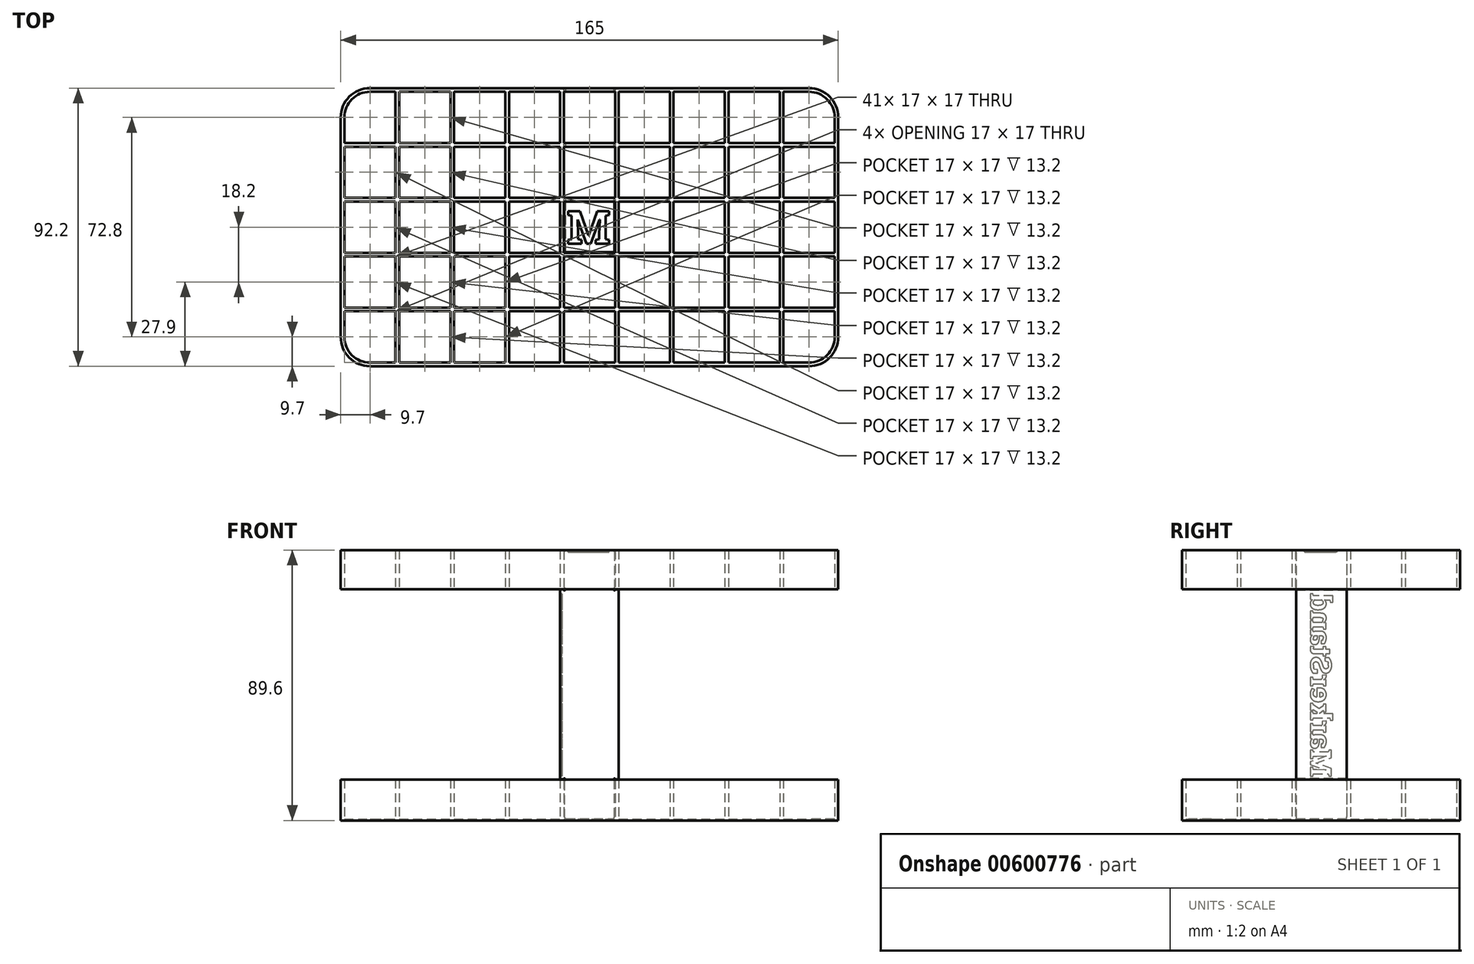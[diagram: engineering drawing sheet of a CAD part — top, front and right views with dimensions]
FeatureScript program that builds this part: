
annotation { "Feature Type Name" : "Feature", "Feature Type Description" : "" }
export const myFeature = defineFeature(function(context is Context, id is Id, definition is map)
    precondition{}
    {
        {
            var Q0;
            Q0=qCreatedBy(makeId("Top.planeOp"),FACE);
            var sketch = newSketch(context, id + "F0", { "sketchPlane" : qUnion([Q0])});
            skLineSegment(sketch, "E0.bottom", {"start": v(-82.5, 46.1) * mm, "end": v(82.5, 46.1) * mm});
            skLineSegment(sketch, "E0.top", {"start": v(-82.5, -46.1) * mm, "end": v(82.5, -46.1) * mm});
            skLineSegment(sketch, "E0.left", {"start": v(-82.5, 46.1) * mm, "end": v(-82.5, -46.1) * mm});
            skLineSegment(sketch, "E0.right", {"start": v(82.5, 46.1) * mm, "end": v(82.5, -46.1) * mm});
            skPoint(sketch, "E0.middle", {"position": v(0, 0) * mm});
            skLineSegment(sketch, "E1.bottom", {"start": v(-81.3, -44.9) * mm, "end": v(-64.3, -44.9) * mm});
            skLineSegment(sketch, "E1.top", {"start": v(-81.3, -27.9) * mm, "end": v(-64.3, -27.9) * mm});
            skLineSegment(sketch, "E1.left", {"start": v(-81.3, -44.9) * mm, "end": v(-81.3, -27.9) * mm});
            skLineSegment(sketch, "E1.right", {"start": v(-64.3, -44.9) * mm, "end": v(-64.3, -27.9) * mm});
            skLineSegment(sketch, "E2.0.1.0", {"start": v(-64.3, -26.7) * mm, "end": v(-64.3, -9.7) * mm});
            skLineSegment(sketch, "E2.0.1.1", {"start": v(-81.3, -26.7) * mm, "end": v(-64.3, -26.7) * mm});
            skLineSegment(sketch, "E2.0.1.2", {"start": v(-81.3, -26.7) * mm, "end": v(-81.3, -9.7) * mm});
            skLineSegment(sketch, "E2.0.1.3", {"start": v(-81.3, -9.7) * mm, "end": v(-64.3, -9.7) * mm});
            skLineSegment(sketch, "E2.0.2.0", {"start": v(-64.3, -8.5) * mm, "end": v(-64.3, 8.5) * mm});
            skLineSegment(sketch, "E2.0.2.1", {"start": v(-81.3, -8.5) * mm, "end": v(-64.3, -8.5) * mm});
            skLineSegment(sketch, "E2.0.2.2", {"start": v(-81.3, -8.5) * mm, "end": v(-81.3, 8.5) * mm});
            skLineSegment(sketch, "E2.0.2.3", {"start": v(-81.3, 8.5) * mm, "end": v(-64.3, 8.5) * mm});
            skLineSegment(sketch, "E2.0.3.0", {"start": v(-64.3, 9.7) * mm, "end": v(-64.3, 26.7) * mm});
            skLineSegment(sketch, "E2.0.3.1", {"start": v(-81.3, 9.7) * mm, "end": v(-64.3, 9.7) * mm});
            skLineSegment(sketch, "E2.0.3.2", {"start": v(-81.3, 9.7) * mm, "end": v(-81.3, 26.7) * mm});
            skLineSegment(sketch, "E2.0.3.3", {"start": v(-81.3, 26.7) * mm, "end": v(-64.3, 26.7) * mm});
            skLineSegment(sketch, "E2.0.4.0", {"start": v(-64.3, 27.9) * mm, "end": v(-64.3, 44.9) * mm});
            skLineSegment(sketch, "E2.0.4.1", {"start": v(-81.3, 27.9) * mm, "end": v(-64.3, 27.9) * mm});
            skLineSegment(sketch, "E2.0.4.2", {"start": v(-81.3, 27.9) * mm, "end": v(-81.3, 44.9) * mm});
            skLineSegment(sketch, "E2.0.4.3", {"start": v(-81.3, 44.9) * mm, "end": v(-64.3, 44.9) * mm});
            skLineSegment(sketch, "E2.1.0.0", {"start": v(-46.1, -44.9) * mm, "end": v(-46.1, -27.9) * mm});
            skLineSegment(sketch, "E2.1.0.1", {"start": v(-63.1, -44.9) * mm, "end": v(-46.1, -44.9) * mm});
            skLineSegment(sketch, "E2.1.0.2", {"start": v(-63.1, -44.9) * mm, "end": v(-63.1, -27.9) * mm});
            skLineSegment(sketch, "E2.1.0.3", {"start": v(-63.1, -27.9) * mm, "end": v(-46.1, -27.9) * mm});
            skLineSegment(sketch, "E2.1.1.0", {"start": v(-46.1, -26.7) * mm, "end": v(-46.1, -9.7) * mm});
            skLineSegment(sketch, "E2.1.1.1", {"start": v(-63.1, -26.7) * mm, "end": v(-46.1, -26.7) * mm});
            skLineSegment(sketch, "E2.1.1.2", {"start": v(-63.1, -26.7) * mm, "end": v(-63.1, -9.7) * mm});
            skLineSegment(sketch, "E2.1.1.3", {"start": v(-63.1, -9.7) * mm, "end": v(-46.1, -9.7) * mm});
            skLineSegment(sketch, "E2.1.2.0", {"start": v(-46.1, -8.5) * mm, "end": v(-46.1, 8.5) * mm});
            skLineSegment(sketch, "E2.1.2.1", {"start": v(-63.1, -8.5) * mm, "end": v(-46.1, -8.5) * mm});
            skLineSegment(sketch, "E2.1.2.2", {"start": v(-63.1, -8.5) * mm, "end": v(-63.1, 8.5) * mm});
            skLineSegment(sketch, "E2.1.2.3", {"start": v(-63.1, 8.5) * mm, "end": v(-46.1, 8.5) * mm});
            skLineSegment(sketch, "E2.1.3.0", {"start": v(-46.1, 9.7) * mm, "end": v(-46.1, 26.7) * mm});
            skLineSegment(sketch, "E2.1.3.1", {"start": v(-63.1, 9.7) * mm, "end": v(-46.1, 9.7) * mm});
            skLineSegment(sketch, "E2.1.3.2", {"start": v(-63.1, 9.7) * mm, "end": v(-63.1, 26.7) * mm});
            skLineSegment(sketch, "E2.1.3.3", {"start": v(-63.1, 26.7) * mm, "end": v(-46.1, 26.7) * mm});
            skLineSegment(sketch, "E2.1.4.0", {"start": v(-46.1, 27.9) * mm, "end": v(-46.1, 44.9) * mm});
            skLineSegment(sketch, "E2.1.4.1", {"start": v(-63.1, 27.9) * mm, "end": v(-46.1, 27.9) * mm});
            skLineSegment(sketch, "E2.1.4.2", {"start": v(-63.1, 27.9) * mm, "end": v(-63.1, 44.9) * mm});
            skLineSegment(sketch, "E2.1.4.3", {"start": v(-63.1, 44.9) * mm, "end": v(-46.1, 44.9) * mm});
            skLineSegment(sketch, "E2.2.0.0", {"start": v(-27.9, -44.9) * mm, "end": v(-27.9, -27.9) * mm});
            skLineSegment(sketch, "E2.2.0.1", {"start": v(-44.9, -44.9) * mm, "end": v(-27.9, -44.9) * mm});
            skLineSegment(sketch, "E2.2.0.2", {"start": v(-44.9, -44.9) * mm, "end": v(-44.9, -27.9) * mm});
            skLineSegment(sketch, "E2.2.0.3", {"start": v(-44.9, -27.9) * mm, "end": v(-27.9, -27.9) * mm});
            skLineSegment(sketch, "E2.2.1.0", {"start": v(-27.9, -26.7) * mm, "end": v(-27.9, -9.7) * mm});
            skLineSegment(sketch, "E2.2.1.1", {"start": v(-44.9, -26.7) * mm, "end": v(-27.9, -26.7) * mm});
            skLineSegment(sketch, "E2.2.1.2", {"start": v(-44.9, -26.7) * mm, "end": v(-44.9, -9.7) * mm});
            skLineSegment(sketch, "E2.2.1.3", {"start": v(-44.9, -9.7) * mm, "end": v(-27.9, -9.7) * mm});
            skLineSegment(sketch, "E2.2.2.0", {"start": v(-27.9, -8.5) * mm, "end": v(-27.9, 8.5) * mm});
            skLineSegment(sketch, "E2.2.2.1", {"start": v(-44.9, -8.5) * mm, "end": v(-27.9, -8.5) * mm});
            skLineSegment(sketch, "E2.2.2.2", {"start": v(-44.9, -8.5) * mm, "end": v(-44.9, 8.5) * mm});
            skLineSegment(sketch, "E2.2.2.3", {"start": v(-44.9, 8.5) * mm, "end": v(-27.9, 8.5) * mm});
            skLineSegment(sketch, "E2.2.3.0", {"start": v(-27.9, 9.7) * mm, "end": v(-27.9, 26.7) * mm});
            skLineSegment(sketch, "E2.2.3.1", {"start": v(-44.9, 9.7) * mm, "end": v(-27.9, 9.7) * mm});
            skLineSegment(sketch, "E2.2.3.2", {"start": v(-44.9, 9.7) * mm, "end": v(-44.9, 26.7) * mm});
            skLineSegment(sketch, "E2.2.3.3", {"start": v(-44.9, 26.7) * mm, "end": v(-27.9, 26.7) * mm});
            skLineSegment(sketch, "E2.2.4.0", {"start": v(-27.9, 27.9) * mm, "end": v(-27.9, 44.9) * mm});
            skLineSegment(sketch, "E2.2.4.1", {"start": v(-44.9, 27.9) * mm, "end": v(-27.9, 27.9) * mm});
            skLineSegment(sketch, "E2.2.4.2", {"start": v(-44.9, 27.9) * mm, "end": v(-44.9, 44.9) * mm});
            skLineSegment(sketch, "E2.2.4.3", {"start": v(-44.9, 44.9) * mm, "end": v(-27.9, 44.9) * mm});
            skLineSegment(sketch, "E2.3.0.0", {"start": v(-9.7, -44.9) * mm, "end": v(-9.7, -27.9) * mm});
            skLineSegment(sketch, "E2.3.0.1", {"start": v(-26.7, -44.9) * mm, "end": v(-9.7, -44.9) * mm});
            skLineSegment(sketch, "E2.3.0.2", {"start": v(-26.7, -44.9) * mm, "end": v(-26.7, -27.9) * mm});
            skLineSegment(sketch, "E2.3.0.3", {"start": v(-26.7, -27.9) * mm, "end": v(-9.7, -27.9) * mm});
            skLineSegment(sketch, "E2.3.1.0", {"start": v(-9.7, -26.7) * mm, "end": v(-9.7, -9.7) * mm});
            skLineSegment(sketch, "E2.3.1.1", {"start": v(-26.7, -26.7) * mm, "end": v(-9.7, -26.7) * mm});
            skLineSegment(sketch, "E2.3.1.2", {"start": v(-26.7, -26.7) * mm, "end": v(-26.7, -9.7) * mm});
            skLineSegment(sketch, "E2.3.1.3", {"start": v(-26.7, -9.7) * mm, "end": v(-9.7, -9.7) * mm});
            skLineSegment(sketch, "E2.3.2.0", {"start": v(-9.7, -8.5) * mm, "end": v(-9.7, 8.5) * mm});
            skLineSegment(sketch, "E2.3.2.1", {"start": v(-26.7, -8.5) * mm, "end": v(-9.7, -8.5) * mm});
            skLineSegment(sketch, "E2.3.2.2", {"start": v(-26.7, -8.5) * mm, "end": v(-26.7, 8.5) * mm});
            skLineSegment(sketch, "E2.3.2.3", {"start": v(-26.7, 8.5) * mm, "end": v(-9.7, 8.5) * mm});
            skLineSegment(sketch, "E2.3.3.0", {"start": v(-9.7, 9.7) * mm, "end": v(-9.7, 26.7) * mm});
            skLineSegment(sketch, "E2.3.3.1", {"start": v(-26.7, 9.7) * mm, "end": v(-9.7, 9.7) * mm});
            skLineSegment(sketch, "E2.3.3.2", {"start": v(-26.7, 9.7) * mm, "end": v(-26.7, 26.7) * mm});
            skLineSegment(sketch, "E2.3.3.3", {"start": v(-26.7, 26.7) * mm, "end": v(-9.7, 26.7) * mm});
            skLineSegment(sketch, "E2.3.4.0", {"start": v(-9.7, 27.9) * mm, "end": v(-9.7, 44.9) * mm});
            skLineSegment(sketch, "E2.3.4.1", {"start": v(-26.7, 27.9) * mm, "end": v(-9.7, 27.9) * mm});
            skLineSegment(sketch, "E2.3.4.2", {"start": v(-26.7, 27.9) * mm, "end": v(-26.7, 44.9) * mm});
            skLineSegment(sketch, "E2.3.4.3", {"start": v(-26.7, 44.9) * mm, "end": v(-9.7, 44.9) * mm});
            skLineSegment(sketch, "E2.4.0.0", {"start": v(8.5, -44.9) * mm, "end": v(8.5, -27.9) * mm});
            skLineSegment(sketch, "E2.4.0.1", {"start": v(-8.5, -44.9) * mm, "end": v(8.5, -44.9) * mm});
            skLineSegment(sketch, "E2.4.0.2", {"start": v(-8.5, -44.9) * mm, "end": v(-8.5, -27.9) * mm});
            skLineSegment(sketch, "E2.4.0.3", {"start": v(-8.5, -27.9) * mm, "end": v(8.5, -27.9) * mm});
            skLineSegment(sketch, "E2.4.1.0", {"start": v(8.5, -26.7) * mm, "end": v(8.5, -9.7) * mm});
            skLineSegment(sketch, "E2.4.1.1", {"start": v(-8.5, -26.7) * mm, "end": v(8.5, -26.7) * mm});
            skLineSegment(sketch, "E2.4.1.2", {"start": v(-8.5, -26.7) * mm, "end": v(-8.5, -9.7) * mm});
            skLineSegment(sketch, "E2.4.1.3", {"start": v(-8.5, -9.7) * mm, "end": v(8.5, -9.7) * mm});
            skLineSegment(sketch, "E2.4.2.0", {"start": v(8.5, -8.5) * mm, "end": v(8.5, 8.5) * mm});
            skLineSegment(sketch, "E2.4.2.1", {"start": v(-8.5, -8.5) * mm, "end": v(8.5, -8.5) * mm});
            skLineSegment(sketch, "E2.4.2.2", {"start": v(-8.5, -8.5) * mm, "end": v(-8.5, 8.5) * mm});
            skLineSegment(sketch, "E2.4.2.3", {"start": v(-8.5, 8.5) * mm, "end": v(8.5, 8.5) * mm});
            skLineSegment(sketch, "E2.4.3.0", {"start": v(8.5, 9.7) * mm, "end": v(8.5, 26.7) * mm});
            skLineSegment(sketch, "E2.4.3.1", {"start": v(-8.5, 9.7) * mm, "end": v(8.5, 9.7) * mm});
            skLineSegment(sketch, "E2.4.3.2", {"start": v(-8.5, 9.7) * mm, "end": v(-8.5, 26.7) * mm});
            skLineSegment(sketch, "E2.4.3.3", {"start": v(-8.5, 26.7) * mm, "end": v(8.5, 26.7) * mm});
            skLineSegment(sketch, "E2.4.4.0", {"start": v(8.5, 27.9) * mm, "end": v(8.5, 44.9) * mm});
            skLineSegment(sketch, "E2.4.4.1", {"start": v(-8.5, 27.9) * mm, "end": v(8.5, 27.9) * mm});
            skLineSegment(sketch, "E2.4.4.2", {"start": v(-8.5, 27.9) * mm, "end": v(-8.5, 44.9) * mm});
            skLineSegment(sketch, "E2.4.4.3", {"start": v(-8.5, 44.9) * mm, "end": v(8.5, 44.9) * mm});
            skLineSegment(sketch, "E2.5.0.0", {"start": v(26.7, -44.9) * mm, "end": v(26.7, -27.9) * mm});
            skLineSegment(sketch, "E2.5.0.1", {"start": v(9.7, -44.9) * mm, "end": v(26.7, -44.9) * mm});
            skLineSegment(sketch, "E2.5.0.2", {"start": v(9.7, -44.9) * mm, "end": v(9.7, -27.9) * mm});
            skLineSegment(sketch, "E2.5.0.3", {"start": v(9.7, -27.9) * mm, "end": v(26.7, -27.9) * mm});
            skLineSegment(sketch, "E2.5.1.0", {"start": v(26.7, -26.7) * mm, "end": v(26.7, -9.7) * mm});
            skLineSegment(sketch, "E2.5.1.1", {"start": v(9.7, -26.7) * mm, "end": v(26.7, -26.7) * mm});
            skLineSegment(sketch, "E2.5.1.2", {"start": v(9.7, -26.7) * mm, "end": v(9.7, -9.7) * mm});
            skLineSegment(sketch, "E2.5.1.3", {"start": v(9.7, -9.7) * mm, "end": v(26.7, -9.7) * mm});
            skLineSegment(sketch, "E2.5.2.0", {"start": v(26.7, -8.5) * mm, "end": v(26.7, 8.5) * mm});
            skLineSegment(sketch, "E2.5.2.1", {"start": v(9.7, -8.5) * mm, "end": v(26.7, -8.5) * mm});
            skLineSegment(sketch, "E2.5.2.2", {"start": v(9.7, -8.5) * mm, "end": v(9.7, 8.5) * mm});
            skLineSegment(sketch, "E2.5.2.3", {"start": v(9.7, 8.5) * mm, "end": v(26.7, 8.5) * mm});
            skLineSegment(sketch, "E2.5.3.0", {"start": v(26.7, 9.7) * mm, "end": v(26.7, 26.7) * mm});
            skLineSegment(sketch, "E2.5.3.1", {"start": v(9.7, 9.7) * mm, "end": v(26.7, 9.7) * mm});
            skLineSegment(sketch, "E2.5.3.2", {"start": v(9.7, 9.7) * mm, "end": v(9.7, 26.7) * mm});
            skLineSegment(sketch, "E2.5.3.3", {"start": v(9.7, 26.7) * mm, "end": v(26.7, 26.7) * mm});
            skLineSegment(sketch, "E2.5.4.0", {"start": v(26.7, 27.9) * mm, "end": v(26.7, 44.9) * mm});
            skLineSegment(sketch, "E2.5.4.1", {"start": v(9.7, 27.9) * mm, "end": v(26.7, 27.9) * mm});
            skLineSegment(sketch, "E2.5.4.2", {"start": v(9.7, 27.9) * mm, "end": v(9.7, 44.9) * mm});
            skLineSegment(sketch, "E2.5.4.3", {"start": v(9.7, 44.9) * mm, "end": v(26.7, 44.9) * mm});
            skLineSegment(sketch, "E2.6.0.0", {"start": v(44.9, -44.9) * mm, "end": v(44.9, -27.9) * mm});
            skLineSegment(sketch, "E2.6.0.1", {"start": v(27.9, -44.9) * mm, "end": v(44.9, -44.9) * mm});
            skLineSegment(sketch, "E2.6.0.2", {"start": v(27.9, -44.9) * mm, "end": v(27.9, -27.9) * mm});
            skLineSegment(sketch, "E2.6.0.3", {"start": v(27.9, -27.9) * mm, "end": v(44.9, -27.9) * mm});
            skLineSegment(sketch, "E2.6.1.0", {"start": v(44.9, -26.7) * mm, "end": v(44.9, -9.7) * mm});
            skLineSegment(sketch, "E2.6.1.1", {"start": v(27.9, -26.7) * mm, "end": v(44.9, -26.7) * mm});
            skLineSegment(sketch, "E2.6.1.2", {"start": v(27.9, -26.7) * mm, "end": v(27.9, -9.7) * mm});
            skLineSegment(sketch, "E2.6.1.3", {"start": v(27.9, -9.7) * mm, "end": v(44.9, -9.7) * mm});
            skLineSegment(sketch, "E2.6.2.0", {"start": v(44.9, -8.5) * mm, "end": v(44.9, 8.5) * mm});
            skLineSegment(sketch, "E2.6.2.1", {"start": v(27.9, -8.5) * mm, "end": v(44.9, -8.5) * mm});
            skLineSegment(sketch, "E2.6.2.2", {"start": v(27.9, -8.5) * mm, "end": v(27.9, 8.5) * mm});
            skLineSegment(sketch, "E2.6.2.3", {"start": v(27.9, 8.5) * mm, "end": v(44.9, 8.5) * mm});
            skLineSegment(sketch, "E2.6.3.0", {"start": v(44.9, 9.7) * mm, "end": v(44.9, 26.7) * mm});
            skLineSegment(sketch, "E2.6.3.1", {"start": v(27.9, 9.7) * mm, "end": v(44.9, 9.7) * mm});
            skLineSegment(sketch, "E2.6.3.2", {"start": v(27.9, 9.7) * mm, "end": v(27.9, 26.7) * mm});
            skLineSegment(sketch, "E2.6.3.3", {"start": v(27.9, 26.7) * mm, "end": v(44.9, 26.7) * mm});
            skLineSegment(sketch, "E2.6.4.0", {"start": v(44.9, 27.9) * mm, "end": v(44.9, 44.9) * mm});
            skLineSegment(sketch, "E2.6.4.1", {"start": v(27.9, 27.9) * mm, "end": v(44.9, 27.9) * mm});
            skLineSegment(sketch, "E2.6.4.2", {"start": v(27.9, 27.9) * mm, "end": v(27.9, 44.9) * mm});
            skLineSegment(sketch, "E2.6.4.3", {"start": v(27.9, 44.9) * mm, "end": v(44.9, 44.9) * mm});
            skLineSegment(sketch, "E2.7.0.0", {"start": v(63.1, -44.9) * mm, "end": v(63.1, -27.9) * mm});
            skLineSegment(sketch, "E2.7.0.1", {"start": v(46.1, -44.9) * mm, "end": v(63.1, -44.9) * mm});
            skLineSegment(sketch, "E2.7.0.2", {"start": v(46.1, -44.9) * mm, "end": v(46.1, -27.9) * mm});
            skLineSegment(sketch, "E2.7.0.3", {"start": v(46.1, -27.9) * mm, "end": v(63.1, -27.9) * mm});
            skLineSegment(sketch, "E2.7.1.0", {"start": v(63.1, -26.7) * mm, "end": v(63.1, -9.7) * mm});
            skLineSegment(sketch, "E2.7.1.1", {"start": v(46.1, -26.7) * mm, "end": v(63.1, -26.7) * mm});
            skLineSegment(sketch, "E2.7.1.2", {"start": v(46.1, -26.7) * mm, "end": v(46.1, -9.7) * mm});
            skLineSegment(sketch, "E2.7.1.3", {"start": v(46.1, -9.7) * mm, "end": v(63.1, -9.7) * mm});
            skLineSegment(sketch, "E2.7.2.0", {"start": v(63.1, -8.5) * mm, "end": v(63.1, 8.5) * mm});
            skLineSegment(sketch, "E2.7.2.1", {"start": v(46.1, -8.5) * mm, "end": v(63.1, -8.5) * mm});
            skLineSegment(sketch, "E2.7.2.2", {"start": v(46.1, -8.5) * mm, "end": v(46.1, 8.5) * mm});
            skLineSegment(sketch, "E2.7.2.3", {"start": v(46.1, 8.5) * mm, "end": v(63.1, 8.5) * mm});
            skLineSegment(sketch, "E2.7.3.0", {"start": v(63.1, 9.7) * mm, "end": v(63.1, 26.7) * mm});
            skLineSegment(sketch, "E2.7.3.1", {"start": v(46.1, 9.7) * mm, "end": v(63.1, 9.7) * mm});
            skLineSegment(sketch, "E2.7.3.2", {"start": v(46.1, 9.7) * mm, "end": v(46.1, 26.7) * mm});
            skLineSegment(sketch, "E2.7.3.3", {"start": v(46.1, 26.7) * mm, "end": v(63.1, 26.7) * mm});
            skLineSegment(sketch, "E2.7.4.0", {"start": v(63.1, 27.9) * mm, "end": v(63.1, 44.9) * mm});
            skLineSegment(sketch, "E2.7.4.1", {"start": v(46.1, 27.9) * mm, "end": v(63.1, 27.9) * mm});
            skLineSegment(sketch, "E2.7.4.2", {"start": v(46.1, 27.9) * mm, "end": v(46.1, 44.9) * mm});
            skLineSegment(sketch, "E2.7.4.3", {"start": v(46.1, 44.9) * mm, "end": v(63.1, 44.9) * mm});
            skLineSegment(sketch, "E2.8.0.0", {"start": v(81.3, -44.9) * mm, "end": v(81.3, -27.9) * mm});
            skLineSegment(sketch, "E2.8.0.1", {"start": v(64.3, -44.9) * mm, "end": v(81.3, -44.9) * mm});
            skLineSegment(sketch, "E2.8.0.2", {"start": v(64.3, -44.9) * mm, "end": v(64.3, -27.9) * mm});
            skLineSegment(sketch, "E2.8.0.3", {"start": v(64.3, -27.9) * mm, "end": v(81.3, -27.9) * mm});
            skLineSegment(sketch, "E2.8.1.0", {"start": v(81.3, -26.7) * mm, "end": v(81.3, -9.7) * mm});
            skLineSegment(sketch, "E2.8.1.1", {"start": v(64.3, -26.7) * mm, "end": v(81.3, -26.7) * mm});
            skLineSegment(sketch, "E2.8.1.2", {"start": v(64.3, -26.7) * mm, "end": v(64.3, -9.7) * mm});
            skLineSegment(sketch, "E2.8.1.3", {"start": v(64.3, -9.7) * mm, "end": v(81.3, -9.7) * mm});
            skLineSegment(sketch, "E2.8.2.0", {"start": v(81.3, -8.5) * mm, "end": v(81.3, 8.5) * mm});
            skLineSegment(sketch, "E2.8.2.1", {"start": v(64.3, -8.5) * mm, "end": v(81.3, -8.5) * mm});
            skLineSegment(sketch, "E2.8.2.2", {"start": v(64.3, -8.5) * mm, "end": v(64.3, 8.5) * mm});
            skLineSegment(sketch, "E2.8.2.3", {"start": v(64.3, 8.5) * mm, "end": v(81.3, 8.5) * mm});
            skLineSegment(sketch, "E2.8.3.0", {"start": v(81.3, 9.7) * mm, "end": v(81.3, 26.7) * mm});
            skLineSegment(sketch, "E2.8.3.1", {"start": v(64.3, 9.7) * mm, "end": v(81.3, 9.7) * mm});
            skLineSegment(sketch, "E2.8.3.2", {"start": v(64.3, 9.7) * mm, "end": v(64.3, 26.7) * mm});
            skLineSegment(sketch, "E2.8.3.3", {"start": v(64.3, 26.7) * mm, "end": v(81.3, 26.7) * mm});
            skLineSegment(sketch, "E2.8.4.0", {"start": v(81.3, 27.9) * mm, "end": v(81.3, 44.9) * mm});
            skLineSegment(sketch, "E2.8.4.1", {"start": v(64.3, 27.9) * mm, "end": v(81.3, 27.9) * mm});
            skLineSegment(sketch, "E2.8.4.2", {"start": v(64.3, 27.9) * mm, "end": v(64.3, 44.9) * mm});
            skLineSegment(sketch, "E2.8.4.3", {"start": v(64.3, 44.9) * mm, "end": v(81.3, 44.9) * mm});
            skLineSegment(sketch, "E2.direction1", {"start": v(-46.1, -54) * mm, "end": v(-27.9, -54) * mm, "construction": true});
            skLineSegment(sketch, "E2.direction2", {"start": v(-46.1, -54) * mm, "end": v(-46.1, -35.8) * mm, "construction": true});
            skSolve(sketch);
        }
        {
            var Q0;
            Q0 = qSketchRegion(id + "F0", true);
            extrude(context, id + "F1", {"entities" : qUnion([Q0]), "depth" : 13.6 * mm, "offsetDistance" : 25 * mm});
        }
        {
            var Q0;
            Q0=qCreatedBy(makeId("Top.planeOp"),FACE);
            var sketch = newSketch(context, id + "F2", { "sketchPlane" : qUnion([Q0])});
            skLineSegment(sketch, "E3.0", {"start": v(-82.5, 46.1) * mm, "end": v(82.5, 46.1) * mm});
            skLineSegment(sketch, "E4.0", {"start": v(-82.5, 46.1) * mm, "end": v(-82.5, -46.1) * mm});
            skLineSegment(sketch, "E5.0", {"start": v(-82.5, -46.1) * mm, "end": v(82.5, -46.1) * mm});
            skLineSegment(sketch, "E6.0", {"start": v(82.5, 46.1) * mm, "end": v(82.5, -46.1) * mm});
            skSolve(sketch);
        }
        {
            var Q0;
            Q0 = qSketchRegion(id + "F2", true);
            extrude(context, id + "F3", {"entities" : qUnion([Q0]), "operationType" : NewBodyOperationType.ADD, "depth" : 0.4 * mm, "offsetDistance" : 25 * mm});
        }
        {
            var Q0;
            Q0=makeQuery(id+"F1.opExtrude","SWEPT_EDGE",EDGE,{"disambiguationData":[OSD([sQuery(id+"F0.wireOp",EDGE,"E1.bottom"),sQuery(id+"F0.wireOp",EDGE,"E1.left")])]});
            var Q1;
            Q1=makeQuery(id+"F1.opExtrude","SWEPT_EDGE",EDGE,{"disambiguationData":[OSD([sQuery(id+"F0.wireOp",EDGE,"E2.0.4.2"),sQuery(id+"F0.wireOp",EDGE,"E2.0.4.3")])]});
            var Q2;
            Q2=makeQuery(id+"F1.opExtrude","SWEPT_EDGE",EDGE,{"disambiguationData":[OSD([sQuery(id+"F0.wireOp",EDGE,"E2.8.0.0"),sQuery(id+"F0.wireOp",EDGE,"E2.8.0.1")])]});
            var Q3;
            Q3=makeQuery(id+"F1.opExtrude","SWEPT_EDGE",EDGE,{"disambiguationData":[OSD([sQuery(id+"F0.wireOp",EDGE,"E2.8.4.0"),sQuery(id+"F0.wireOp",EDGE,"E2.8.4.3")])]});
            fillet(context, id + "F4", {"entities" : qUnion([Q0, Q1, Q2, Q3]), "radius" : 8.5 * mm, "tangentPropagation" : true, "allowEdgeOverflow" : false});
        }
        {
            var Q0;
            Q0=makeQuery(id+"F1.opExtrude","SWEPT_EDGE",EDGE,{"disambiguationData":[OSD([sQuery(id+"F0.wireOp",EDGE,"E0.top"),sQuery(id+"F0.wireOp",EDGE,"E0.left")])]});
            var Q1;
            Q1=makeQuery(id+"F1.opExtrude","SWEPT_EDGE",EDGE,{"disambiguationData":[OSD([sQuery(id+"F0.wireOp",EDGE,"E0.bottom"),sQuery(id+"F0.wireOp",EDGE,"E0.left")])]});
            var Q2;
            Q2=makeQuery(id+"F1.opExtrude","SWEPT_EDGE",EDGE,{"disambiguationData":[OSD([sQuery(id+"F0.wireOp",EDGE,"E0.top"),sQuery(id+"F0.wireOp",EDGE,"E0.right")])]});
            var Q3;
            Q3=makeQuery(id+"F1.opExtrude","SWEPT_EDGE",EDGE,{"disambiguationData":[OSD([sQuery(id+"F0.wireOp",EDGE,"E0.bottom"),sQuery(id+"F0.wireOp",EDGE,"E0.right")])]});
            fillet(context, id + "F5", {"entities" : qUnion([Q0, Q1, Q2, Q3]), "radius" : 9.7 * mm, "tangentPropagation" : true, "allowEdgeOverflow" : false});
        }
        {
            var Q0;
            Q0=makeQuery(id+"F1.opExtrude","SWEPT_FACE",FACE,{"disambiguationData":[OSD([sQuery(id+"F0.wireOp",EDGE,"E2.4.2.3")])]});
            var sketch = newSketch(context, id + "F6", { "sketchPlane" : qUnion([Q0])});
            skLineSegment(sketch, "E7", {"start": v(-9.7, 76.6) * mm, "end": v(-9.7, 13.6) * mm});
            skLineSegment(sketch, "E8", {"start": v(-9.7, 13.6) * mm, "end": v(-8.3, 13.6) * mm});
            skLineSegment(sketch, "E9", {"start": v(-8.3, 13.6) * mm, "end": v(-8.3, 0.6) * mm});
            skLineSegment(sketch, "E10", {"start": v(-8.3, 0.6) * mm, "end": v(8.3, 0.6) * mm});
            skLineSegment(sketch, "E11", {"start": v(8.3, 0.6) * mm, "end": v(8.3, 13.6) * mm});
            skLineSegment(sketch, "E12", {"start": v(8.3, 13.6) * mm, "end": v(9.7, 13.6) * mm});
            skLineSegment(sketch, "E13", {"start": v(9.7, 13.6) * mm, "end": v(9.7, 76.6) * mm});
            skLineSegment(sketch, "E14", {"start": v(-9.7, 45.1) * mm, "end": v(9.7, 45.1) * mm, "construction": true});
            skLineSegment(sketch, "E15.MirrorCS", {"start": v(-9.7, 76.6) * mm, "end": v(-8.3, 76.6) * mm});
            skLineSegment(sketch, "E16.MirrorCS", {"start": v(-8.3, 76.6) * mm, "end": v(-8.3, 89.6) * mm});
            skLineSegment(sketch, "E17.MirrorCS", {"start": v(-8.3, 89.6) * mm, "end": v(8.3, 89.6) * mm});
            skLineSegment(sketch, "E18.MirrorCS", {"start": v(8.3, 89.6) * mm, "end": v(8.3, 76.6) * mm});
            skLineSegment(sketch, "E19.MirrorCS", {"start": v(8.3, 76.6) * mm, "end": v(9.7, 76.6) * mm});
            skSolve(sketch);
        }
        {
            var Q0;
            Q0 = qSketchRegion(id + "F6", true);
            extrude(context, id + "F7", {"entities" : qUnion([Q0]), "depth" : 16.8 * mm, "offsetDistance" : 25 * mm});
        }
        {
            var Q0;
            Q0=makeQuery(id+"F7.opExtrude","CAP_FACE",FACE,{"disambiguationData":[OSD([sQuery(id+"F6.wireOp",EDGE,"E7"),sQuery(id+"F6.wireOp",EDGE,"E8"),sQuery(id+"F6.wireOp",EDGE,"E9"),sQuery(id+"F6.wireOp",EDGE,"E10"),sQuery(id+"F6.wireOp",EDGE,"E11"),sQuery(id+"F6.wireOp",EDGE,"E12"),sQuery(id+"F6.wireOp",EDGE,"E13"),sQuery(id+"F6.wireOp",EDGE,"E15.MirrorCS"),sQuery(id+"F6.wireOp",EDGE,"E16.MirrorCS"),sQuery(id+"F6.wireOp",EDGE,"E17.MirrorCS"),sQuery(id+"F6.wireOp",EDGE,"E18.MirrorCS"),sQuery(id+"F6.wireOp",EDGE,"E19.MirrorCS")])],"isStart":false});
            var sketch = newSketch(context, id + "F8", { "sketchPlane" : qUnion([Q0])});
            skCircle(sketch, "E20", {"center": v(-8.3, 76.6) * mm, "radius": 0.3 * mm});
            skCircle(sketch, "E21", {"center": v(8.3, 76.6) * mm, "radius": 0.3 * mm});
            skCircle(sketch, "E22", {"center": v(8.3, 13.6) * mm, "radius": 0.3 * mm});
            skCircle(sketch, "E23", {"center": v(-8.3, 13.6) * mm, "radius": 0.3 * mm});
            skSolve(sketch);
        }
        {
            var Q0;
            Q0 = qSketchRegion(id + "F8", true);
            extrude(context, id + "F9", {"entities" : qUnion([Q0]), "operationType" : NewBodyOperationType.REMOVE, "endBound" : BoundingType.THROUGH_ALL, "oppositeDirection" : true, "depth" : 25 * mm, "offsetDistance" : 25 * mm});
        }
        {
            var Q0;
            Q0=makeQuery(id+"F9.boolean.opBoolean","INTERSECT",EDGE,{"derivedFrom":[makeQuery(id+"F7.opExtrude","SWEPT_FACE",FACE,{"disambiguationData":[OSD([sQuery(id+"F6.wireOp",EDGE,"E15.MirrorCS")])]}),makeQuery(id+"F9.opExtrude","SWEPT_FACE",FACE,{"disambiguationData":[OSD([sQuery(id+"F8.wireOp",EDGE,"E20")])]})]});
            var Q1;
            Q1=makeQuery(id+"F9.boolean.opBoolean","INTERSECT",EDGE,{"derivedFrom":[makeQuery(id+"F7.opExtrude","SWEPT_FACE",FACE,{"disambiguationData":[OSD([sQuery(id+"F6.wireOp",EDGE,"E16.MirrorCS")])]}),makeQuery(id+"F9.opExtrude","SWEPT_FACE",FACE,{"disambiguationData":[OSD([sQuery(id+"F8.wireOp",EDGE,"E20")])]})]});
            var Q2;
            Q2=makeQuery(id+"F7.opExtrude","SWEPT_EDGE",EDGE,{"disambiguationData":[OSD([sQuery(id+"F6.wireOp",EDGE,"E7"),sQuery(id+"F6.wireOp",EDGE,"E15.MirrorCS")])]});
            var Q3;
            Q3=makeQuery(id+"F7.opExtrude","SWEPT_EDGE",EDGE,{"disambiguationData":[OSD([sQuery(id+"F6.wireOp",EDGE,"E16.MirrorCS"),sQuery(id+"F6.wireOp",EDGE,"E17.MirrorCS")])]});
            var Q4;
            Q4=makeQuery(id+"F7.opExtrude","SWEPT_EDGE",EDGE,{"disambiguationData":[OSD([sQuery(id+"F6.wireOp",EDGE,"E13"),sQuery(id+"F6.wireOp",EDGE,"E19.MirrorCS")])]});
            var Q5;
            Q5=makeQuery(id+"F7.opExtrude","SWEPT_EDGE",EDGE,{"disambiguationData":[OSD([sQuery(id+"F6.wireOp",EDGE,"E17.MirrorCS"),sQuery(id+"F6.wireOp",EDGE,"E18.MirrorCS")])]});
            var Q6;
            Q6=makeQuery(id+"F9.boolean.opBoolean","INTERSECT",EDGE,{"derivedFrom":[makeQuery(id+"F7.opExtrude","SWEPT_FACE",FACE,{"disambiguationData":[OSD([sQuery(id+"F6.wireOp",EDGE,"E19.MirrorCS")])]}),makeQuery(id+"F9.opExtrude","SWEPT_FACE",FACE,{"disambiguationData":[OSD([sQuery(id+"F8.wireOp",EDGE,"E21")])]})]});
            var Q7;
            Q7=makeQuery(id+"F9.boolean.opBoolean","INTERSECT",EDGE,{"derivedFrom":[makeQuery(id+"F7.opExtrude","SWEPT_FACE",FACE,{"disambiguationData":[OSD([sQuery(id+"F6.wireOp",EDGE,"E18.MirrorCS")])]}),makeQuery(id+"F9.opExtrude","SWEPT_FACE",FACE,{"disambiguationData":[OSD([sQuery(id+"F8.wireOp",EDGE,"E21")])]})]});
            var Q8;
            Q8=makeQuery(id+"F7.opExtrude","SWEPT_EDGE",EDGE,{"disambiguationData":[OSD([sQuery(id+"F6.wireOp",EDGE,"E10"),sQuery(id+"F6.wireOp",EDGE,"E11")])]});
            var Q9;
            Q9=makeQuery(id+"F7.opExtrude","SWEPT_EDGE",EDGE,{"disambiguationData":[OSD([sQuery(id+"F6.wireOp",EDGE,"E9"),sQuery(id+"F6.wireOp",EDGE,"E10")])]});
            var Q10;
            Q10=makeQuery(id+"F9.boolean.opBoolean","INTERSECT",EDGE,{"derivedFrom":[makeQuery(id+"F7.opExtrude","SWEPT_FACE",FACE,{"disambiguationData":[OSD([sQuery(id+"F6.wireOp",EDGE,"E9")])]}),makeQuery(id+"F9.opExtrude","SWEPT_FACE",FACE,{"disambiguationData":[OSD([sQuery(id+"F8.wireOp",EDGE,"E23")])]})]});
            var Q11;
            Q11=makeQuery(id+"F9.boolean.opBoolean","INTERSECT",EDGE,{"derivedFrom":[makeQuery(id+"F7.opExtrude","SWEPT_FACE",FACE,{"disambiguationData":[OSD([sQuery(id+"F6.wireOp",EDGE,"E8")])]}),makeQuery(id+"F9.opExtrude","SWEPT_FACE",FACE,{"disambiguationData":[OSD([sQuery(id+"F8.wireOp",EDGE,"E23")])]})]});
            var Q12;
            Q12=makeQuery(id+"F7.opExtrude","SWEPT_EDGE",EDGE,{"disambiguationData":[OSD([sQuery(id+"F6.wireOp",EDGE,"E7"),sQuery(id+"F6.wireOp",EDGE,"E8")])]});
            var Q13;
            Q13=makeQuery(id+"F9.boolean.opBoolean","INTERSECT",EDGE,{"derivedFrom":[makeQuery(id+"F7.opExtrude","SWEPT_FACE",FACE,{"disambiguationData":[OSD([sQuery(id+"F6.wireOp",EDGE,"E12")])]}),makeQuery(id+"F9.opExtrude","SWEPT_FACE",FACE,{"disambiguationData":[OSD([sQuery(id+"F8.wireOp",EDGE,"E22")])]})]});
            var Q14;
            Q14=makeQuery(id+"F9.boolean.opBoolean","INTERSECT",EDGE,{"derivedFrom":[makeQuery(id+"F7.opExtrude","SWEPT_FACE",FACE,{"disambiguationData":[OSD([sQuery(id+"F6.wireOp",EDGE,"E11")])]}),makeQuery(id+"F9.opExtrude","SWEPT_FACE",FACE,{"disambiguationData":[OSD([sQuery(id+"F8.wireOp",EDGE,"E22")])]})]});
            var Q15;
            Q15=makeQuery(id+"F7.opExtrude","SWEPT_EDGE",EDGE,{"disambiguationData":[OSD([sQuery(id+"F6.wireOp",EDGE,"E12"),sQuery(id+"F6.wireOp",EDGE,"E13")])]});
            fillet(context, id + "F10", {"entities" : qUnion([Q0, Q1, Q2, Q3, Q4, Q5, Q6, Q7, Q8, Q9, Q10, Q11, Q12, Q13, Q14, Q15]), "radius" : 0.6 * mm, "tangentPropagation" : true, "allowEdgeOverflow" : false});
        }
        {
            var Q0;
            Q0=makeQuery(id+"F7.opExtrude","SWEPT_FACE",FACE,{"disambiguationData":[OSD([sQuery(id+"F6.wireOp",EDGE,"E7")])]});
            var sketch = newSketch(context, id + "F11", { "sketchPlane" : qUnion([Q0])});
            skLineSegment(sketch, "E24", {"start": v(-0.1, 76) * mm, "end": v(-0.1, 14.2) * mm, "construction": true});
            skLineSegment(sketch, "E25", {"start": v(-8.5, 45.1) * mm, "end": v(8.3, 45.1) * mm, "construction": true});
            skText(sketch, "E26", { "text": "MarkerStand", "fontName": "RobotoSlab-Bold.ttf"});
            const initialGuessF11  = {"E26": [0.00354, 0.0144, 0, 1, 0.00704]};
            skSetInitialGuess(sketch, initialGuessF11);
            skSolve(sketch);
        }
        {
            var Q0;
            Q0 = qSketchRegion(id + "F11", true);
            extrude(context, id + "F12", {"entities" : qUnion([Q0]), "operationType" : NewBodyOperationType.REMOVE, "depth" : -0.6 * mm, "offsetDistance" : 25 * mm});
        }
        {
            var Q0;
            Q0=makeQuery(id+"F7.opExtrude","SWEPT_FACE",FACE,{"disambiguationData":[OSD([sQuery(id+"F6.wireOp",EDGE,"E17.MirrorCS")])]});
            var sketch = newSketch(context, id + "F13", { "sketchPlane" : qUnion([Q0])});
            skText(sketch, "E27", { "text": "M", "fontName": "RobotoSlab-Bold.ttf"});
            const initialGuessF13  = {"E27": [-0.0075, -0.00552, 1, 0, 0.01102]};
            skSetInitialGuess(sketch, initialGuessF13);
            skSolve(sketch);
        }
        {
            var Q0;
            Q0 = qSketchRegion(id + "F13", true);
            extrude(context, id + "F14", {"entities" : qUnion([Q0]), "operationType" : NewBodyOperationType.REMOVE, "oppositeDirection" : true, "depth" : 0.6 * mm, "offsetDistance" : 25 * mm});
        }
        {
            var Q0;
            Q0=makeQuery(id+"F7.opExtrude","SWEPT_FACE",FACE,{"disambiguationData":[OSD([sQuery(id+"F6.wireOp",EDGE,"E19.MirrorCS")])]});
            var sketch = newSketch(context, id + "F15", { "sketchPlane" : qUnion([Q0])});
            skLineSegment(sketch, "E28.bottom", {"start": v(-82.5, -46.1) * mm, "end": v(82.5, -46.1) * mm});
            skLineSegment(sketch, "E28.top", {"start": v(-82.5, 46.1) * mm, "end": v(82.5, 46.1) * mm});
            skLineSegment(sketch, "E28.left", {"start": v(-82.5, -46.1) * mm, "end": v(-82.5, 46.1) * mm});
            skLineSegment(sketch, "E28.right", {"start": v(82.5, -46.1) * mm, "end": v(82.5, 46.1) * mm});
            skPoint(sketch, "E28.middle", {"position": v(0, 0) * mm});
            skLineSegment(sketch, "E29.bottom", {"start": v(-64.3, -27.9) * mm, "end": v(-81.3, -27.9) * mm});
            skLineSegment(sketch, "E29.top", {"start": v(-64.3, -44.9) * mm, "end": v(-81.3, -44.9) * mm});
            skLineSegment(sketch, "E29.left", {"start": v(-64.3, -27.9) * mm, "end": v(-64.3, -44.9) * mm});
            skLineSegment(sketch, "E29.right", {"start": v(-81.3, -27.9) * mm, "end": v(-81.3, -44.9) * mm});
            skLineSegment(sketch, "E30.0.1.0", {"start": v(-64.3, -26.7) * mm, "end": v(-81.3, -26.7) * mm});
            skLineSegment(sketch, "E30.0.1.1", {"start": v(-81.3, -9.7) * mm, "end": v(-81.3, -26.7) * mm});
            skLineSegment(sketch, "E30.0.1.2", {"start": v(-64.3, -9.7) * mm, "end": v(-81.3, -9.7) * mm});
            skLineSegment(sketch, "E30.0.1.3", {"start": v(-64.3, -9.7) * mm, "end": v(-64.3, -26.7) * mm});
            skLineSegment(sketch, "E30.0.2.0", {"start": v(-64.3, -8.5) * mm, "end": v(-81.3, -8.5) * mm});
            skLineSegment(sketch, "E30.0.2.1", {"start": v(-81.3, 8.5) * mm, "end": v(-81.3, -8.5) * mm});
            skLineSegment(sketch, "E30.0.2.2", {"start": v(-64.3, 8.5) * mm, "end": v(-81.3, 8.5) * mm});
            skLineSegment(sketch, "E30.0.2.3", {"start": v(-64.3, 8.5) * mm, "end": v(-64.3, -8.5) * mm});
            skLineSegment(sketch, "E30.0.3.0", {"start": v(-64.3, 9.7) * mm, "end": v(-81.3, 9.7) * mm});
            skLineSegment(sketch, "E30.0.3.1", {"start": v(-81.3, 26.7) * mm, "end": v(-81.3, 9.7) * mm});
            skLineSegment(sketch, "E30.0.3.2", {"start": v(-64.3, 26.7) * mm, "end": v(-81.3, 26.7) * mm});
            skLineSegment(sketch, "E30.0.3.3", {"start": v(-64.3, 26.7) * mm, "end": v(-64.3, 9.7) * mm});
            skLineSegment(sketch, "E30.0.4.0", {"start": v(-64.3, 27.9) * mm, "end": v(-81.3, 27.9) * mm});
            skLineSegment(sketch, "E30.0.4.1", {"start": v(-81.3, 44.9) * mm, "end": v(-81.3, 27.9) * mm});
            skLineSegment(sketch, "E30.0.4.2", {"start": v(-64.3, 44.9) * mm, "end": v(-81.3, 44.9) * mm});
            skLineSegment(sketch, "E30.0.4.3", {"start": v(-64.3, 44.9) * mm, "end": v(-64.3, 27.9) * mm});
            skLineSegment(sketch, "E30.1.0.0", {"start": v(-46.1, -44.9) * mm, "end": v(-63.1, -44.9) * mm});
            skLineSegment(sketch, "E30.1.0.1", {"start": v(-63.1, -27.9) * mm, "end": v(-63.1, -44.9) * mm});
            skLineSegment(sketch, "E30.1.0.2", {"start": v(-46.1, -27.9) * mm, "end": v(-63.1, -27.9) * mm});
            skLineSegment(sketch, "E30.1.0.3", {"start": v(-46.1, -27.9) * mm, "end": v(-46.1, -44.9) * mm});
            skLineSegment(sketch, "E30.1.1.0", {"start": v(-46.1, -26.7) * mm, "end": v(-63.1, -26.7) * mm});
            skLineSegment(sketch, "E30.1.1.1", {"start": v(-63.1, -9.7) * mm, "end": v(-63.1, -26.7) * mm});
            skLineSegment(sketch, "E30.1.1.2", {"start": v(-46.1, -9.7) * mm, "end": v(-63.1, -9.7) * mm});
            skLineSegment(sketch, "E30.1.1.3", {"start": v(-46.1, -9.7) * mm, "end": v(-46.1, -26.7) * mm});
            skLineSegment(sketch, "E30.1.2.0", {"start": v(-46.1, -8.5) * mm, "end": v(-63.1, -8.5) * mm});
            skLineSegment(sketch, "E30.1.2.1", {"start": v(-63.1, 8.5) * mm, "end": v(-63.1, -8.5) * mm});
            skLineSegment(sketch, "E30.1.2.2", {"start": v(-46.1, 8.5) * mm, "end": v(-63.1, 8.5) * mm});
            skLineSegment(sketch, "E30.1.2.3", {"start": v(-46.1, 8.5) * mm, "end": v(-46.1, -8.5) * mm});
            skLineSegment(sketch, "E30.1.3.0", {"start": v(-46.1, 9.7) * mm, "end": v(-63.1, 9.7) * mm});
            skLineSegment(sketch, "E30.1.3.1", {"start": v(-63.1, 26.7) * mm, "end": v(-63.1, 9.7) * mm});
            skLineSegment(sketch, "E30.1.3.2", {"start": v(-46.1, 26.7) * mm, "end": v(-63.1, 26.7) * mm});
            skLineSegment(sketch, "E30.1.3.3", {"start": v(-46.1, 26.7) * mm, "end": v(-46.1, 9.7) * mm});
            skLineSegment(sketch, "E30.1.4.0", {"start": v(-46.1, 27.9) * mm, "end": v(-63.1, 27.9) * mm});
            skLineSegment(sketch, "E30.1.4.1", {"start": v(-63.1, 44.9) * mm, "end": v(-63.1, 27.9) * mm});
            skLineSegment(sketch, "E30.1.4.2", {"start": v(-46.1, 44.9) * mm, "end": v(-63.1, 44.9) * mm});
            skLineSegment(sketch, "E30.1.4.3", {"start": v(-46.1, 44.9) * mm, "end": v(-46.1, 27.9) * mm});
            skLineSegment(sketch, "E30.2.0.0", {"start": v(-27.9, -44.9) * mm, "end": v(-44.9, -44.9) * mm});
            skLineSegment(sketch, "E30.2.0.1", {"start": v(-44.9, -27.9) * mm, "end": v(-44.9, -44.9) * mm});
            skLineSegment(sketch, "E30.2.0.2", {"start": v(-27.9, -27.9) * mm, "end": v(-44.9, -27.9) * mm});
            skLineSegment(sketch, "E30.2.0.3", {"start": v(-27.9, -27.9) * mm, "end": v(-27.9, -44.9) * mm});
            skLineSegment(sketch, "E30.2.1.0", {"start": v(-27.9, -26.7) * mm, "end": v(-44.9, -26.7) * mm});
            skLineSegment(sketch, "E30.2.1.1", {"start": v(-44.9, -9.7) * mm, "end": v(-44.9, -26.7) * mm});
            skLineSegment(sketch, "E30.2.1.2", {"start": v(-27.9, -9.7) * mm, "end": v(-44.9, -9.7) * mm});
            skLineSegment(sketch, "E30.2.1.3", {"start": v(-27.9, -9.7) * mm, "end": v(-27.9, -26.7) * mm});
            skLineSegment(sketch, "E30.2.2.0", {"start": v(-27.9, -8.5) * mm, "end": v(-44.9, -8.5) * mm});
            skLineSegment(sketch, "E30.2.2.1", {"start": v(-44.9, 8.5) * mm, "end": v(-44.9, -8.5) * mm});
            skLineSegment(sketch, "E30.2.2.2", {"start": v(-27.9, 8.5) * mm, "end": v(-44.9, 8.5) * mm});
            skLineSegment(sketch, "E30.2.2.3", {"start": v(-27.9, 8.5) * mm, "end": v(-27.9, -8.5) * mm});
            skLineSegment(sketch, "E30.2.3.0", {"start": v(-27.9, 9.7) * mm, "end": v(-44.9, 9.7) * mm});
            skLineSegment(sketch, "E30.2.3.1", {"start": v(-44.9, 26.7) * mm, "end": v(-44.9, 9.7) * mm});
            skLineSegment(sketch, "E30.2.3.2", {"start": v(-27.9, 26.7) * mm, "end": v(-44.9, 26.7) * mm});
            skLineSegment(sketch, "E30.2.3.3", {"start": v(-27.9, 26.7) * mm, "end": v(-27.9, 9.7) * mm});
            skLineSegment(sketch, "E30.2.4.0", {"start": v(-27.9, 27.9) * mm, "end": v(-44.9, 27.9) * mm});
            skLineSegment(sketch, "E30.2.4.1", {"start": v(-44.9, 44.9) * mm, "end": v(-44.9, 27.9) * mm});
            skLineSegment(sketch, "E30.2.4.2", {"start": v(-27.9, 44.9) * mm, "end": v(-44.9, 44.9) * mm});
            skLineSegment(sketch, "E30.2.4.3", {"start": v(-27.9, 44.9) * mm, "end": v(-27.9, 27.9) * mm});
            skLineSegment(sketch, "E30.3.0.0", {"start": v(-9.7, -44.9) * mm, "end": v(-26.7, -44.9) * mm});
            skLineSegment(sketch, "E30.3.0.1", {"start": v(-26.7, -27.9) * mm, "end": v(-26.7, -44.9) * mm});
            skLineSegment(sketch, "E30.3.0.2", {"start": v(-9.7, -27.9) * mm, "end": v(-26.7, -27.9) * mm});
            skLineSegment(sketch, "E30.3.0.3", {"start": v(-9.7, -27.9) * mm, "end": v(-9.7, -44.9) * mm});
            skLineSegment(sketch, "E30.3.1.0", {"start": v(-9.7, -26.7) * mm, "end": v(-26.7, -26.7) * mm});
            skLineSegment(sketch, "E30.3.1.1", {"start": v(-26.7, -9.7) * mm, "end": v(-26.7, -26.7) * mm});
            skLineSegment(sketch, "E30.3.1.2", {"start": v(-9.7, -9.7) * mm, "end": v(-26.7, -9.7) * mm});
            skLineSegment(sketch, "E30.3.1.3", {"start": v(-9.7, -9.7) * mm, "end": v(-9.7, -26.7) * mm});
            skLineSegment(sketch, "E30.3.2.0", {"start": v(-9.7, -8.5) * mm, "end": v(-26.7, -8.5) * mm});
            skLineSegment(sketch, "E30.3.2.1", {"start": v(-26.7, 8.5) * mm, "end": v(-26.7, -8.5) * mm});
            skLineSegment(sketch, "E30.3.2.2", {"start": v(-9.7, 8.5) * mm, "end": v(-26.7, 8.5) * mm});
            skLineSegment(sketch, "E30.3.2.3", {"start": v(-9.7, 8.5) * mm, "end": v(-9.7, -8.5) * mm});
            skLineSegment(sketch, "E30.3.3.0", {"start": v(-9.7, 9.7) * mm, "end": v(-26.7, 9.7) * mm});
            skLineSegment(sketch, "E30.3.3.1", {"start": v(-26.7, 26.7) * mm, "end": v(-26.7, 9.7) * mm});
            skLineSegment(sketch, "E30.3.3.2", {"start": v(-9.7, 26.7) * mm, "end": v(-26.7, 26.7) * mm});
            skLineSegment(sketch, "E30.3.3.3", {"start": v(-9.7, 26.7) * mm, "end": v(-9.7, 9.7) * mm});
            skLineSegment(sketch, "E30.3.4.0", {"start": v(-9.7, 27.9) * mm, "end": v(-26.7, 27.9) * mm});
            skLineSegment(sketch, "E30.3.4.1", {"start": v(-26.7, 44.9) * mm, "end": v(-26.7, 27.9) * mm});
            skLineSegment(sketch, "E30.3.4.2", {"start": v(-9.7, 44.9) * mm, "end": v(-26.7, 44.9) * mm});
            skLineSegment(sketch, "E30.3.4.3", {"start": v(-9.7, 44.9) * mm, "end": v(-9.7, 27.9) * mm});
            skLineSegment(sketch, "E30.4.0.0", {"start": v(8.5, -44.9) * mm, "end": v(-8.5, -44.9) * mm});
            skLineSegment(sketch, "E30.4.0.1", {"start": v(-8.5, -27.9) * mm, "end": v(-8.5, -44.9) * mm});
            skLineSegment(sketch, "E30.4.0.2", {"start": v(8.5, -27.9) * mm, "end": v(-8.5, -27.9) * mm});
            skLineSegment(sketch, "E30.4.0.3", {"start": v(8.5, -27.9) * mm, "end": v(8.5, -44.9) * mm});
            skLineSegment(sketch, "E30.4.1.0", {"start": v(8.5, -26.7) * mm, "end": v(-8.5, -26.7) * mm});
            skLineSegment(sketch, "E30.4.1.1", {"start": v(-8.5, -9.7) * mm, "end": v(-8.5, -26.7) * mm});
            skLineSegment(sketch, "E30.4.1.2", {"start": v(8.5, -9.7) * mm, "end": v(-8.5, -9.7) * mm});
            skLineSegment(sketch, "E30.4.1.3", {"start": v(8.5, -9.7) * mm, "end": v(8.5, -26.7) * mm});
            skLineSegment(sketch, "E30.4.2.0", {"start": v(8.5, -8.5) * mm, "end": v(-8.5, -8.5) * mm});
            skLineSegment(sketch, "E30.4.2.1", {"start": v(-8.5, 8.5) * mm, "end": v(-8.5, -8.5) * mm});
            skLineSegment(sketch, "E30.4.2.2", {"start": v(8.5, 8.5) * mm, "end": v(-8.5, 8.5) * mm});
            skLineSegment(sketch, "E30.4.2.3", {"start": v(8.5, 8.5) * mm, "end": v(8.5, -8.5) * mm});
            skLineSegment(sketch, "E30.4.3.0", {"start": v(8.5, 9.7) * mm, "end": v(-8.5, 9.7) * mm});
            skLineSegment(sketch, "E30.4.3.1", {"start": v(-8.5, 26.7) * mm, "end": v(-8.5, 9.7) * mm});
            skLineSegment(sketch, "E30.4.3.2", {"start": v(8.5, 26.7) * mm, "end": v(-8.5, 26.7) * mm});
            skLineSegment(sketch, "E30.4.3.3", {"start": v(8.5, 26.7) * mm, "end": v(8.5, 9.7) * mm});
            skLineSegment(sketch, "E30.4.4.0", {"start": v(8.5, 27.9) * mm, "end": v(-8.5, 27.9) * mm});
            skLineSegment(sketch, "E30.4.4.1", {"start": v(-8.5, 44.9) * mm, "end": v(-8.5, 27.9) * mm});
            skLineSegment(sketch, "E30.4.4.2", {"start": v(8.5, 44.9) * mm, "end": v(-8.5, 44.9) * mm});
            skLineSegment(sketch, "E30.4.4.3", {"start": v(8.5, 44.9) * mm, "end": v(8.5, 27.9) * mm});
            skLineSegment(sketch, "E30.5.0.0", {"start": v(26.7, -44.9) * mm, "end": v(9.7, -44.9) * mm});
            skLineSegment(sketch, "E30.5.0.1", {"start": v(9.7, -27.9) * mm, "end": v(9.7, -44.9) * mm});
            skLineSegment(sketch, "E30.5.0.2", {"start": v(26.7, -27.9) * mm, "end": v(9.7, -27.9) * mm});
            skLineSegment(sketch, "E30.5.0.3", {"start": v(26.7, -27.9) * mm, "end": v(26.7, -44.9) * mm});
            skLineSegment(sketch, "E30.5.1.0", {"start": v(26.7, -26.7) * mm, "end": v(9.7, -26.7) * mm});
            skLineSegment(sketch, "E30.5.1.1", {"start": v(9.7, -9.7) * mm, "end": v(9.7, -26.7) * mm});
            skLineSegment(sketch, "E30.5.1.2", {"start": v(26.7, -9.7) * mm, "end": v(9.7, -9.7) * mm});
            skLineSegment(sketch, "E30.5.1.3", {"start": v(26.7, -9.7) * mm, "end": v(26.7, -26.7) * mm});
            skLineSegment(sketch, "E30.5.2.0", {"start": v(26.7, -8.5) * mm, "end": v(9.7, -8.5) * mm});
            skLineSegment(sketch, "E30.5.2.1", {"start": v(9.7, 8.5) * mm, "end": v(9.7, -8.5) * mm});
            skLineSegment(sketch, "E30.5.2.2", {"start": v(26.7, 8.5) * mm, "end": v(9.7, 8.5) * mm});
            skLineSegment(sketch, "E30.5.2.3", {"start": v(26.7, 8.5) * mm, "end": v(26.7, -8.5) * mm});
            skLineSegment(sketch, "E30.5.3.0", {"start": v(26.7, 9.7) * mm, "end": v(9.7, 9.7) * mm});
            skLineSegment(sketch, "E30.5.3.1", {"start": v(9.7, 26.7) * mm, "end": v(9.7, 9.7) * mm});
            skLineSegment(sketch, "E30.5.3.2", {"start": v(26.7, 26.7) * mm, "end": v(9.7, 26.7) * mm});
            skLineSegment(sketch, "E30.5.3.3", {"start": v(26.7, 26.7) * mm, "end": v(26.7, 9.7) * mm});
            skLineSegment(sketch, "E30.5.4.0", {"start": v(26.7, 27.9) * mm, "end": v(9.7, 27.9) * mm});
            skLineSegment(sketch, "E30.5.4.1", {"start": v(9.7, 44.9) * mm, "end": v(9.7, 27.9) * mm});
            skLineSegment(sketch, "E30.5.4.2", {"start": v(26.7, 44.9) * mm, "end": v(9.7, 44.9) * mm});
            skLineSegment(sketch, "E30.5.4.3", {"start": v(26.7, 44.9) * mm, "end": v(26.7, 27.9) * mm});
            skLineSegment(sketch, "E30.6.0.0", {"start": v(44.9, -44.9) * mm, "end": v(27.9, -44.9) * mm});
            skLineSegment(sketch, "E30.6.0.1", {"start": v(27.9, -27.9) * mm, "end": v(27.9, -44.9) * mm});
            skLineSegment(sketch, "E30.6.0.2", {"start": v(44.9, -27.9) * mm, "end": v(27.9, -27.9) * mm});
            skLineSegment(sketch, "E30.6.0.3", {"start": v(44.9, -27.9) * mm, "end": v(44.9, -44.9) * mm});
            skLineSegment(sketch, "E30.6.1.0", {"start": v(44.9, -26.7) * mm, "end": v(27.9, -26.7) * mm});
            skLineSegment(sketch, "E30.6.1.1", {"start": v(27.9, -9.7) * mm, "end": v(27.9, -26.7) * mm});
            skLineSegment(sketch, "E30.6.1.2", {"start": v(44.9, -9.7) * mm, "end": v(27.9, -9.7) * mm});
            skLineSegment(sketch, "E30.6.1.3", {"start": v(44.9, -9.7) * mm, "end": v(44.9, -26.7) * mm});
            skLineSegment(sketch, "E30.6.2.0", {"start": v(44.9, -8.5) * mm, "end": v(27.9, -8.5) * mm});
            skLineSegment(sketch, "E30.6.2.1", {"start": v(27.9, 8.5) * mm, "end": v(27.9, -8.5) * mm});
            skLineSegment(sketch, "E30.6.2.2", {"start": v(44.9, 8.5) * mm, "end": v(27.9, 8.5) * mm});
            skLineSegment(sketch, "E30.6.2.3", {"start": v(44.9, 8.5) * mm, "end": v(44.9, -8.5) * mm});
            skLineSegment(sketch, "E30.6.3.0", {"start": v(44.9, 9.7) * mm, "end": v(27.9, 9.7) * mm});
            skLineSegment(sketch, "E30.6.3.1", {"start": v(27.9, 26.7) * mm, "end": v(27.9, 9.7) * mm});
            skLineSegment(sketch, "E30.6.3.2", {"start": v(44.9, 26.7) * mm, "end": v(27.9, 26.7) * mm});
            skLineSegment(sketch, "E30.6.3.3", {"start": v(44.9, 26.7) * mm, "end": v(44.9, 9.7) * mm});
            skLineSegment(sketch, "E30.6.4.0", {"start": v(44.9, 27.9) * mm, "end": v(27.9, 27.9) * mm});
            skLineSegment(sketch, "E30.6.4.1", {"start": v(27.9, 44.9) * mm, "end": v(27.9, 27.9) * mm});
            skLineSegment(sketch, "E30.6.4.2", {"start": v(44.9, 44.9) * mm, "end": v(27.9, 44.9) * mm});
            skLineSegment(sketch, "E30.6.4.3", {"start": v(44.9, 44.9) * mm, "end": v(44.9, 27.9) * mm});
            skLineSegment(sketch, "E30.7.0.0", {"start": v(63.1, -44.9) * mm, "end": v(46.1, -44.9) * mm});
            skLineSegment(sketch, "E30.7.0.1", {"start": v(46.1, -27.9) * mm, "end": v(46.1, -44.9) * mm});
            skLineSegment(sketch, "E30.7.0.2", {"start": v(63.1, -27.9) * mm, "end": v(46.1, -27.9) * mm});
            skLineSegment(sketch, "E30.7.0.3", {"start": v(63.1, -27.9) * mm, "end": v(63.1, -44.9) * mm});
            skLineSegment(sketch, "E30.7.1.0", {"start": v(63.1, -26.7) * mm, "end": v(46.1, -26.7) * mm});
            skLineSegment(sketch, "E30.7.1.1", {"start": v(46.1, -9.7) * mm, "end": v(46.1, -26.7) * mm});
            skLineSegment(sketch, "E30.7.1.2", {"start": v(63.1, -9.7) * mm, "end": v(46.1, -9.7) * mm});
            skLineSegment(sketch, "E30.7.1.3", {"start": v(63.1, -9.7) * mm, "end": v(63.1, -26.7) * mm});
            skLineSegment(sketch, "E30.7.2.0", {"start": v(63.1, -8.5) * mm, "end": v(46.1, -8.5) * mm});
            skLineSegment(sketch, "E30.7.2.1", {"start": v(46.1, 8.5) * mm, "end": v(46.1, -8.5) * mm});
            skLineSegment(sketch, "E30.7.2.2", {"start": v(63.1, 8.5) * mm, "end": v(46.1, 8.5) * mm});
            skLineSegment(sketch, "E30.7.2.3", {"start": v(63.1, 8.5) * mm, "end": v(63.1, -8.5) * mm});
            skLineSegment(sketch, "E30.7.3.0", {"start": v(63.1, 9.7) * mm, "end": v(46.1, 9.7) * mm});
            skLineSegment(sketch, "E30.7.3.1", {"start": v(46.1, 26.7) * mm, "end": v(46.1, 9.7) * mm});
            skLineSegment(sketch, "E30.7.3.2", {"start": v(63.1, 26.7) * mm, "end": v(46.1, 26.7) * mm});
            skLineSegment(sketch, "E30.7.3.3", {"start": v(63.1, 26.7) * mm, "end": v(63.1, 9.7) * mm});
            skLineSegment(sketch, "E30.7.4.0", {"start": v(63.1, 27.9) * mm, "end": v(46.1, 27.9) * mm});
            skLineSegment(sketch, "E30.7.4.1", {"start": v(46.1, 44.9) * mm, "end": v(46.1, 27.9) * mm});
            skLineSegment(sketch, "E30.7.4.2", {"start": v(63.1, 44.9) * mm, "end": v(46.1, 44.9) * mm});
            skLineSegment(sketch, "E30.7.4.3", {"start": v(63.1, 44.9) * mm, "end": v(63.1, 27.9) * mm});
            skLineSegment(sketch, "E30.8.0.0", {"start": v(81.3, -44.9) * mm, "end": v(64.3, -44.9) * mm});
            skLineSegment(sketch, "E30.8.0.1", {"start": v(64.3, -27.9) * mm, "end": v(64.3, -44.9) * mm});
            skLineSegment(sketch, "E30.8.0.2", {"start": v(81.3, -27.9) * mm, "end": v(64.3, -27.9) * mm});
            skLineSegment(sketch, "E30.8.0.3", {"start": v(81.3, -27.9) * mm, "end": v(81.3, -44.9) * mm});
            skLineSegment(sketch, "E30.8.1.0", {"start": v(81.3, -26.7) * mm, "end": v(64.3, -26.7) * mm});
            skLineSegment(sketch, "E30.8.1.1", {"start": v(64.3, -9.7) * mm, "end": v(64.3, -26.7) * mm});
            skLineSegment(sketch, "E30.8.1.2", {"start": v(81.3, -9.7) * mm, "end": v(64.3, -9.7) * mm});
            skLineSegment(sketch, "E30.8.1.3", {"start": v(81.3, -9.7) * mm, "end": v(81.3, -26.7) * mm});
            skLineSegment(sketch, "E30.8.2.0", {"start": v(81.3, -8.5) * mm, "end": v(64.3, -8.5) * mm});
            skLineSegment(sketch, "E30.8.2.1", {"start": v(64.3, 8.5) * mm, "end": v(64.3, -8.5) * mm});
            skLineSegment(sketch, "E30.8.2.2", {"start": v(81.3, 8.5) * mm, "end": v(64.3, 8.5) * mm});
            skLineSegment(sketch, "E30.8.2.3", {"start": v(81.3, 8.5) * mm, "end": v(81.3, -8.5) * mm});
            skLineSegment(sketch, "E30.8.3.0", {"start": v(81.3, 9.7) * mm, "end": v(64.3, 9.7) * mm});
            skLineSegment(sketch, "E30.8.3.1", {"start": v(64.3, 26.7) * mm, "end": v(64.3, 9.7) * mm});
            skLineSegment(sketch, "E30.8.3.2", {"start": v(81.3, 26.7) * mm, "end": v(64.3, 26.7) * mm});
            skLineSegment(sketch, "E30.8.3.3", {"start": v(81.3, 26.7) * mm, "end": v(81.3, 9.7) * mm});
            skLineSegment(sketch, "E30.8.4.0", {"start": v(81.3, 27.9) * mm, "end": v(64.3, 27.9) * mm});
            skLineSegment(sketch, "E30.8.4.1", {"start": v(64.3, 44.9) * mm, "end": v(64.3, 27.9) * mm});
            skLineSegment(sketch, "E30.8.4.2", {"start": v(81.3, 44.9) * mm, "end": v(64.3, 44.9) * mm});
            skLineSegment(sketch, "E30.8.4.3", {"start": v(81.3, 44.9) * mm, "end": v(81.3, 27.9) * mm});
            skLineSegment(sketch, "E30.direction1", {"start": v(-81.3, -44.9) * mm, "end": v(-63.1, -44.9) * mm, "construction": true});
            skLineSegment(sketch, "E30.direction2", {"start": v(-81.3, -44.9) * mm, "end": v(-81.3, -26.7) * mm, "construction": true});
            skSolve(sketch);
        }
        {
            var Q0;
            Q0 = qSketchRegion(id + "F15", true);
            extrude(context, id + "F16", {"entities" : qUnion([Q0]), "depth" : 13 * mm, "offsetDistance" : 25 * mm});
        }
        {
            var Q0;
            Q0=makeQuery(id+"F16.opExtrude","SWEPT_EDGE",EDGE,{"disambiguationData":[OSD([sQuery(id+"F15.wireOp",EDGE,"E30.8.4.2"),sQuery(id+"F15.wireOp",EDGE,"E30.8.4.3")])]});
            var Q1;
            Q1=makeQuery(id+"F16.opExtrude","SWEPT_EDGE",EDGE,{"disambiguationData":[OSD([sQuery(id+"F15.wireOp",EDGE,"E30.0.4.1"),sQuery(id+"F15.wireOp",EDGE,"E30.0.4.2")])]});
            var Q2;
            Q2=makeQuery(id+"F16.opExtrude","SWEPT_EDGE",EDGE,{"disambiguationData":[OSD([sQuery(id+"F15.wireOp",EDGE,"E29.top"),sQuery(id+"F15.wireOp",EDGE,"E29.right")])]});
            var Q3;
            Q3=makeQuery(id+"F16.opExtrude","SWEPT_EDGE",EDGE,{"disambiguationData":[OSD([sQuery(id+"F15.wireOp",EDGE,"E30.8.0.0"),sQuery(id+"F15.wireOp",EDGE,"E30.8.0.3")])]});
            fillet(context, id + "F17", {"entities" : qUnion([Q0, Q1, Q2, Q3]), "radius" : 8.5 * mm, "tangentPropagation" : true, "allowEdgeOverflow" : false});
        }
        {
            var Q0;
            Q0=makeQuery(id+"F16.opExtrude","SWEPT_EDGE",EDGE,{"disambiguationData":[OSD([sQuery(id+"F15.wireOp",EDGE,"E28.bottom"),sQuery(id+"F15.wireOp",EDGE,"E28.left")])]});
            var Q1;
            Q1=makeQuery(id+"F16.opExtrude","SWEPT_EDGE",EDGE,{"disambiguationData":[OSD([sQuery(id+"F15.wireOp",EDGE,"E28.top"),sQuery(id+"F15.wireOp",EDGE,"E28.left")])]});
            var Q2;
            Q2=makeQuery(id+"F16.opExtrude","SWEPT_EDGE",EDGE,{"disambiguationData":[OSD([sQuery(id+"F15.wireOp",EDGE,"E28.top"),sQuery(id+"F15.wireOp",EDGE,"E28.right")])]});
            var Q3;
            Q3=makeQuery(id+"F16.opExtrude","SWEPT_EDGE",EDGE,{"disambiguationData":[OSD([sQuery(id+"F15.wireOp",EDGE,"E28.bottom"),sQuery(id+"F15.wireOp",EDGE,"E28.right")])]});
            fillet(context, id + "F18", {"entities" : qUnion([Q0, Q1, Q2, Q3]), "radius" : 9.7 * mm, "tangentPropagation" : true, "allowEdgeOverflow" : false});
        }
    });
